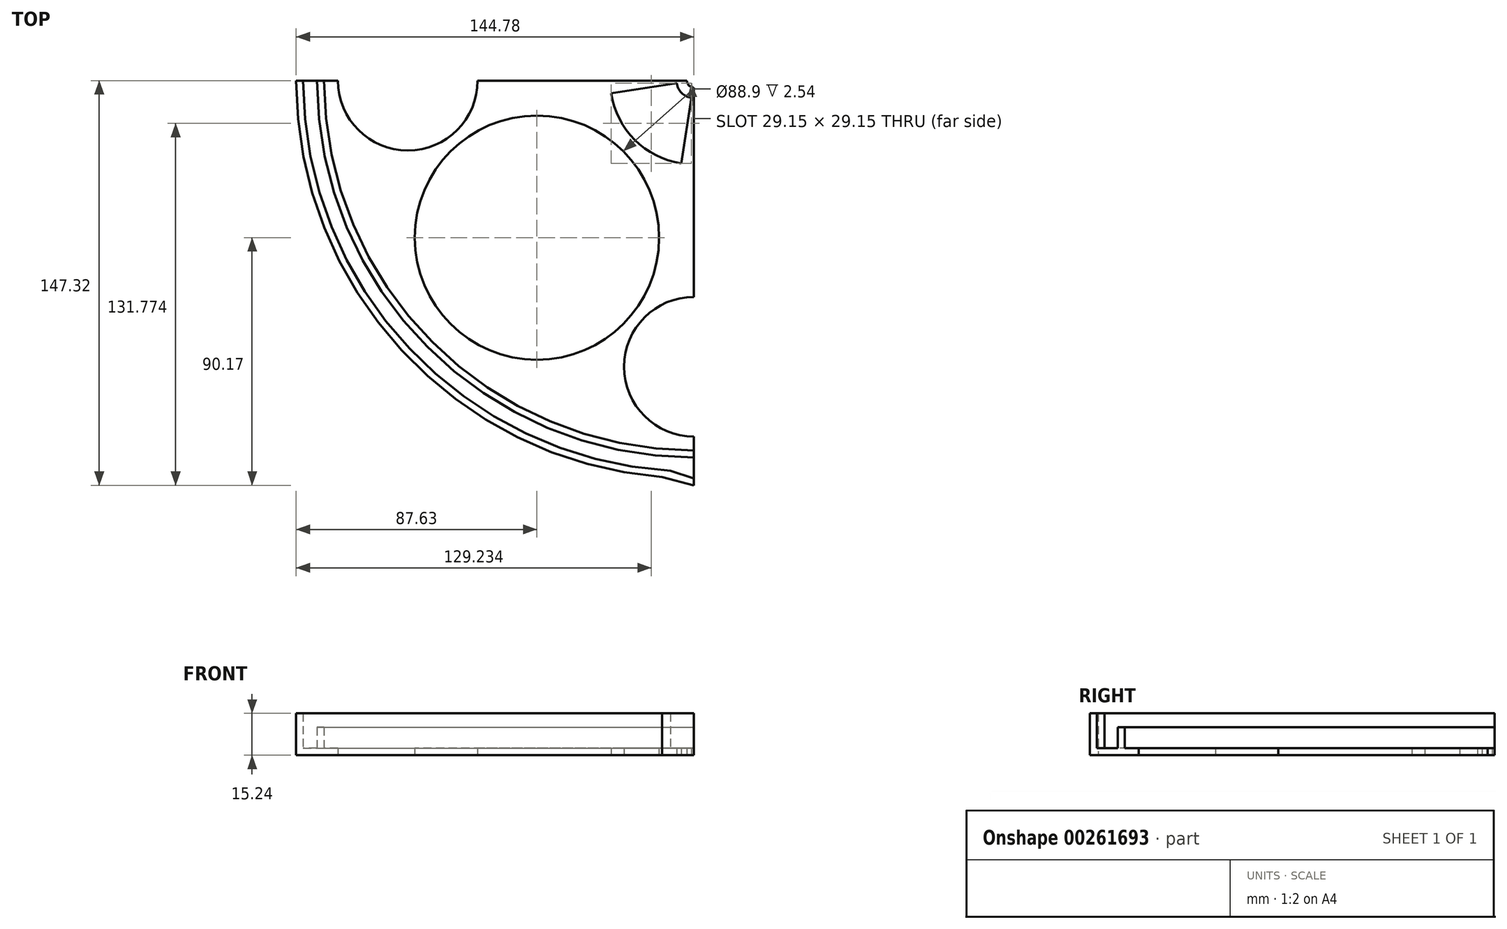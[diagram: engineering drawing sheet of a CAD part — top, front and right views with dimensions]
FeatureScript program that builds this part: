
annotation { "Feature Type Name" : "Feature", "Feature Type Description" : "" }
export const myFeature = defineFeature(function(context is Context, id is Id, definition is map)
    precondition{}
    {
        {
            var Q0;
            Q0=qCreatedBy(makeId("Top.planeOp"),FACE);
            var sketch = newSketch(context, id + "F0", { "sketchPlane" : qUnion([Q0])});
            skCircle(sketch, "E0", {"center": v(0, 0) * mm, "radius": 134.62 * mm});
            skCircle(sketch, "E1.0", {"center": v(0, 0) * mm, "radius": 137.16 * mm});
            skCircle(sketch, "E2.0", {"center": v(0, 0) * mm, "radius": 144.78 * mm});
            skCircle(sketch, "E3.0", {"center": v(0, 0) * mm, "radius": 142.24 * mm});
            skCircle(sketch, "E4.0", {"center": v(0, 0) * mm, "radius": 2.54 * mm});
            skLineSegment(sketch, "E5", {"start": v(0, 0) * mm, "end": v(0, -147.32) * mm});
            skLineSegment(sketch, "E6", {"start": v(-11.57, -144.32) * mm, "end": v(0, -147.32) * mm});
            skFitSpline(sketch, "E7", {"points": [v(0, -147.32) * mm, v(5.92, -144.66) * mm], "startDerivative": vector(10.02, -2.47) * mm, "endDerivative": vector(12.8, 0.33) * mm});
            skLineSegment(sketch, "E8", {"start": v(-8.6, -141.98) * mm, "end": v(0, -144.78) * mm});
            skFitSpline(sketch, "E9", {"points": [v(0, -144.78) * mm, v(4.46, -142.17) * mm], "startDerivative": vector(6.28, -2.02) * mm, "endDerivative": vector(5.88, 0.14) * mm});
            skLineSegment(sketch, "E10", {"start": v(0, 0) * mm, "end": v(-144.78, 0) * mm});
            skLineSegment(sketch, "E11", {"start": v(0, 0) * mm, "end": v(0, 144.78) * mm});
            skLineSegment(sketch, "E12", {"start": v(0, 0) * mm, "end": v(144.78, 0) * mm});
            skLineSegment(sketch, "E13", {"start": v(0, -12.7) * mm, "end": v(-144.22, -12.7) * mm});
            skLineSegment(sketch, "E14", {"start": v(0, -12.7) * mm, "end": v(144.78, -12.7) * mm});
            skLineSegment(sketch, "E15", {"start": v(0, 12.7) * mm, "end": v(-144.22, 12.7) * mm});
            skLineSegment(sketch, "E16", {"start": v(0, 12.7) * mm, "end": v(144.78, 12.7) * mm});
            skLineSegment(sketch, "E17", {"start": v(-12.7, 0) * mm, "end": v(-12.7, 144.22) * mm});
            skLineSegment(sketch, "E18", {"start": v(12.7, 0) * mm, "end": v(12.7, 144.22) * mm});
            skLineSegment(sketch, "E19", {"start": v(-12.7, 0) * mm, "end": v(-12.7, -144.22) * mm});
            skLineSegment(sketch, "E20", {"start": v(12.7, 0) * mm, "end": v(12.7, -144.22) * mm});
            skCircle(sketch, "E21", {"center": v(-57.15, -57.15) * mm, "radius": 44.45 * mm});
            skCircle(sketch, "E22", {"center": v(57.15, -57.15) * mm, "radius": 44.45 * mm});
            skCircle(sketch, "E23", {"center": v(-57.15, 57.15) * mm, "radius": 44.45 * mm});
            skCircle(sketch, "E24", {"center": v(57.15, 57.15) * mm, "radius": 44.45 * mm});
            skCircle(sketch, "E25", {"center": v(-104.14, 0) * mm, "radius": 25.4 * mm});
            skCircle(sketch, "E26", {"center": v(0, 104.14) * mm, "radius": 25.4 * mm});
            skCircle(sketch, "E27", {"center": v(104.14, 0) * mm, "radius": 25.4 * mm});
            skCircle(sketch, "E28", {"center": v(0, -104.14) * mm, "radius": 25.4 * mm});
            skCircle(sketch, "E29", {"center": v(0, 0) * mm, "radius": 30.48 * mm});
            skLineSegment(sketch, "E30", {"start": v(-12.7, -82.14) * mm, "end": v(0, 0) * mm});
            skLineSegment(sketch, "E31", {"start": v(12.7, -82.14) * mm, "end": v(0, 0) * mm});
            skLineSegment(sketch, "E32", {"start": v(82.14, -12.7) * mm, "end": v(0, 0) * mm});
            skLineSegment(sketch, "E33", {"start": v(82.14, 12.7) * mm, "end": v(0, 0) * mm});
            skLineSegment(sketch, "E34", {"start": v(12.7, 82.14) * mm, "end": v(0, 0) * mm});
            skLineSegment(sketch, "E35", {"start": v(-12.7, 82.14) * mm, "end": v(0, 0) * mm});
            skLineSegment(sketch, "E36", {"start": v(-82.14, -12.7) * mm, "end": v(0, 0) * mm});
            skLineSegment(sketch, "E37", {"start": v(-82.14, 12.7) * mm, "end": v(0, 0) * mm});
            skCircle(sketch, "E38", {"center": v(0, 0) * mm, "radius": 6.35 * mm});
            skSolve(sketch);
        }
        {
            var Q0;
            {var subQ0=sQuery(id+"F0.wireOp",EDGE,"E5");var subQ1=sQuery(id+"F0.wireOp",EDGE,"E0");var subQ2=makeQuery(id+"F0.imprint","INTERSECT",VERTEX,{"derivedFrom":[subQ1,subQ0]});Q0=makeQuery(id+"F0.imprint","IMPRINT",FACE,{"disambiguationData":[TD([[makeQuery(id+"F0.imprint","IMPRINT",EDGE,{"disambiguationData":[TD([[subQ2,1.0]])],"derivedFrom":subQ1}),1.0]])]});}
            var Q1;
            {var subQ0=sQuery(id+"F0.wireOp",EDGE,"E13");var subQ1=sQuery(id+"F0.wireOp",EDGE,"E0");var subQ2=makeQuery(id+"F0.imprint","INTERSECT",VERTEX,{"derivedFrom":[subQ1,subQ0]});Q1=makeQuery(id+"F0.imprint","IMPRINT",FACE,{"disambiguationData":[TD([[makeQuery(id+"F0.imprint","IMPRINT",EDGE,{"disambiguationData":[TD([[subQ2,-1.0]])],"derivedFrom":subQ1}),1.0]])]});}
            var Q2;
            {var subQ1=sQuery(id+"F0.wireOp",EDGE,"E10");var subQ3=sQuery(id+"F0.wireOp",EDGE,"E4.0");var subQ4=makeQuery(id+"F0.imprint","INTERSECT",VERTEX,{"derivedFrom":[subQ3,subQ1]});Q2=makeQuery(id+"F0.imprint","IMPRINT",FACE,{"disambiguationData":[TD([[makeQuery(id+"F0.imprint","IMPRINT",EDGE,{"disambiguationData":[TD([[subQ4,-1.0]])],"derivedFrom":subQ3}),-1.0]])]});}
            var Q3;
            {var subQ4=sQuery(id+"F0.wireOp",EDGE,"E10");var subQ6=sQuery(id+"F0.wireOp",EDGE,"E0");var subQ7=makeQuery(id+"F0.imprint","INTERSECT",VERTEX,{"derivedFrom":[subQ6,subQ4]});Q3=makeQuery(id+"F0.imprint","IMPRINT",FACE,{"disambiguationData":[TD([[makeQuery(id+"F0.imprint","IMPRINT",EDGE,{"disambiguationData":[TD([[subQ7,-1.0]])],"derivedFrom":subQ6}),1.0]])]});}
            var Q4;
            {var subQ0=sQuery(id+"F0.wireOp",EDGE,"E29");var subQ1=sQuery(id+"F0.wireOp",EDGE,"E13");var subQ2=makeQuery(id+"F0.imprint","INTERSECT",VERTEX,{"derivedFrom":[subQ1,subQ0]});Q4=makeQuery(id+"F0.imprint","IMPRINT",FACE,{"disambiguationData":[TD([[makeQuery(id+"F0.imprint","IMPRINT",EDGE,{"disambiguationData":[TD([[subQ2,-1.0]])],"derivedFrom":subQ1}),1.0]])]});}
            var Q5;
            {var subQ0=sQuery(id+"F0.wireOp",EDGE,"E29");var subQ1=sQuery(id+"F0.wireOp",EDGE,"E13");var subQ2=makeQuery(id+"F0.imprint","INTERSECT",VERTEX,{"derivedFrom":[subQ1,subQ0]});Q5=makeQuery(id+"F0.imprint","IMPRINT",FACE,{"disambiguationData":[TD([[makeQuery(id+"F0.imprint","IMPRINT",EDGE,{"disambiguationData":[TD([[subQ2,-1.0]])],"derivedFrom":subQ1}),-1.0]])]});}
            var Q6;
            {var subQ0=sQuery(id+"F0.wireOp",EDGE,"E29");var subQ1=sQuery(id+"F0.wireOp",EDGE,"E19");var subQ2=makeQuery(id+"F0.imprint","INTERSECT",VERTEX,{"derivedFrom":[subQ1,subQ0]});Q6=makeQuery(id+"F0.imprint","IMPRINT",FACE,{"disambiguationData":[TD([[makeQuery(id+"F0.imprint","IMPRINT",EDGE,{"disambiguationData":[TD([[subQ2,-1.0]])],"derivedFrom":subQ1}),1.0]])]});}
            var Q7;
            {var subQ0=sQuery(id+"F0.wireOp",EDGE,"E29");var subQ1=sQuery(id+"F0.wireOp",EDGE,"E5");var subQ2=makeQuery(id+"F0.imprint","INTERSECT",VERTEX,{"derivedFrom":[subQ1,subQ0]});Q7=makeQuery(id+"F0.imprint","IMPRINT",FACE,{"disambiguationData":[TD([[makeQuery(id+"F0.imprint","IMPRINT",EDGE,{"disambiguationData":[TD([[subQ2,-1.0]])],"derivedFrom":subQ1}),-1.0]])]});}
            var Q8;
            {var subQ1=sQuery(id+"F0.wireOp",EDGE,"E5");var subQ3=sQuery(id+"F0.wireOp",EDGE,"E29");var subQ4=makeQuery(id+"F0.imprint","INTERSECT",VERTEX,{"derivedFrom":[subQ1,subQ3]});Q8=makeQuery(id+"F0.imprint","IMPRINT",FACE,{"disambiguationData":[TD([[makeQuery(id+"F0.imprint","IMPRINT",EDGE,{"disambiguationData":[TD([[subQ4,1.0]])],"derivedFrom":subQ3}),1.0]])]});}
            var Q9;
            {var subQ0=sQuery(id+"F0.wireOp",EDGE,"E13");var subQ5=sQuery(id+"F0.wireOp",EDGE,"E30");var subQ6=makeQuery(id+"F0.imprint","INTERSECT",VERTEX,{"derivedFrom":[subQ0,subQ5]});Q9=makeQuery(id+"F0.imprint","IMPRINT",FACE,{"disambiguationData":[TD([[makeQuery(id+"F0.imprint","IMPRINT",EDGE,{"disambiguationData":[TD([[subQ6,-1.0]])],"derivedFrom":subQ5}),-1.0]])]});}
            var Q10;
            {var subQ0=sQuery(id+"F0.wireOp",EDGE,"E30");var subQ1=sQuery(id+"F0.wireOp",EDGE,"E4.0");var subQ2=makeQuery(id+"F0.imprint","INTERSECT",VERTEX,{"derivedFrom":[subQ1,subQ0]});Q10=makeQuery(id+"F0.imprint","IMPRINT",FACE,{"disambiguationData":[TD([[makeQuery(id+"F0.imprint","IMPRINT",EDGE,{"disambiguationData":[TD([[subQ2,-1.0]])],"derivedFrom":subQ1}),-1.0]])]});}
            var Q11;
            {var subQ0=sQuery(id+"F0.wireOp",EDGE,"E36");var subQ1=sQuery(id+"F0.wireOp",EDGE,"E4.0");var subQ2=makeQuery(id+"F0.imprint","INTERSECT",VERTEX,{"derivedFrom":[subQ1,subQ0]});Q11=makeQuery(id+"F0.imprint","IMPRINT",FACE,{"disambiguationData":[TD([[makeQuery(id+"F0.imprint","IMPRINT",EDGE,{"disambiguationData":[TD([[subQ2,-1.0]])],"derivedFrom":subQ1}),-1.0]])]});}
            var Q12;
            {var subQ1=sQuery(id+"F0.wireOp",EDGE,"E10");var subQ3=sQuery(id+"F0.wireOp",EDGE,"E29");var subQ4=makeQuery(id+"F0.imprint","INTERSECT",VERTEX,{"derivedFrom":[subQ1,subQ3]});Q12=makeQuery(id+"F0.imprint","IMPRINT",FACE,{"disambiguationData":[TD([[makeQuery(id+"F0.imprint","IMPRINT",EDGE,{"disambiguationData":[TD([[subQ4,-1.0]])],"derivedFrom":subQ3}),1.0]])]});}
            var Q13;
            {var subQ0=sQuery(id+"F0.wireOp",EDGE,"E19");var subQ5=sQuery(id+"F0.wireOp",EDGE,"E36");var subQ6=makeQuery(id+"F0.imprint","INTERSECT",VERTEX,{"derivedFrom":[subQ0,subQ5]});Q13=makeQuery(id+"F0.imprint","IMPRINT",FACE,{"disambiguationData":[TD([[makeQuery(id+"F0.imprint","IMPRINT",EDGE,{"disambiguationData":[TD([[subQ6,-1.0]])],"derivedFrom":subQ5}),1.0]])]});}
            var Q14;
            {var subQ0=sQuery(id+"F0.wireOp",EDGE,"E29");var subQ1=sQuery(id+"F0.wireOp",EDGE,"E10");var subQ2=makeQuery(id+"F0.imprint","INTERSECT",VERTEX,{"derivedFrom":[subQ1,subQ0]});Q14=makeQuery(id+"F0.imprint","IMPRINT",FACE,{"disambiguationData":[TD([[makeQuery(id+"F0.imprint","IMPRINT",EDGE,{"disambiguationData":[TD([[subQ2,-1.0]])],"derivedFrom":subQ1}),1.0]])]});}
            extrude(context, id + "F1", {"entities" : qUnion([Q0, Q1, Q2, Q3, Q4, Q5, Q6, Q7, Q8, Q9, Q10, Q11, Q12, Q13, Q14]), "depth" : 2.54 * mm});
        }
        {
            var Q0;
            {var subQ0=sQuery(id+"F0.wireOp",EDGE,"E5");var subQ1=sQuery(id+"F0.wireOp",EDGE,"E0");var subQ2=makeQuery(id+"F0.imprint","INTERSECT",VERTEX,{"derivedFrom":[subQ1,subQ0]});Q0=makeQuery(id+"F0.imprint","IMPRINT",FACE,{"disambiguationData":[TD([[makeQuery(id+"F0.imprint","IMPRINT",EDGE,{"disambiguationData":[TD([[subQ2,1.0]])],"derivedFrom":subQ1}),-1.0]])]});}
            var Q1;
            {var subQ0=sQuery(id+"F0.wireOp",EDGE,"E13");var subQ1=sQuery(id+"F0.wireOp",EDGE,"E0");var subQ2=makeQuery(id+"F0.imprint","INTERSECT",VERTEX,{"derivedFrom":[subQ1,subQ0]});Q1=makeQuery(id+"F0.imprint","IMPRINT",FACE,{"disambiguationData":[TD([[makeQuery(id+"F0.imprint","IMPRINT",EDGE,{"disambiguationData":[TD([[subQ2,-1.0]])],"derivedFrom":subQ1}),-1.0]])]});}
            var Q2;
            {var subQ0=sQuery(id+"F0.wireOp",EDGE,"E10");var subQ1=sQuery(id+"F0.wireOp",EDGE,"E0");var subQ2=makeQuery(id+"F0.imprint","INTERSECT",VERTEX,{"derivedFrom":[subQ1,subQ0]});Q2=makeQuery(id+"F0.imprint","IMPRINT",FACE,{"disambiguationData":[TD([[makeQuery(id+"F0.imprint","IMPRINT",EDGE,{"disambiguationData":[TD([[subQ2,-1.0]])],"derivedFrom":subQ1}),-1.0]])]});}
            extrude(context, id + "F2", {"entities" : qUnion([Q0, Q1, Q2]), "operationType" : NewBodyOperationType.ADD, "depth" : 10.16 * mm});
        }
        {
            var Q0;
            {var subQ0=sQuery(id+"F0.wireOp",EDGE,"E5");var subQ1=sQuery(id+"F0.wireOp",EDGE,"E1.0");var subQ2=makeQuery(id+"F0.imprint","INTERSECT",VERTEX,{"derivedFrom":[subQ1,subQ0]});Q0=makeQuery(id+"F0.imprint","IMPRINT",FACE,{"disambiguationData":[TD([[makeQuery(id+"F0.imprint","IMPRINT",EDGE,{"disambiguationData":[TD([[subQ2,1.0]])],"derivedFrom":subQ1}),-1.0]])]});}
            var Q1;
            {var subQ0=sQuery(id+"F0.wireOp",EDGE,"E8");Q1=makeQuery(id+"F0.imprint","IMPRINT",FACE,{"disambiguationData":[TD([[makeQuery(id+"F0.imprint","IMPRINT",EDGE,{"derivedFrom":subQ0}),1.0]])]});}
            var Q2;
            {var subQ0=sQuery(id+"F0.wireOp",EDGE,"E13");var subQ1=sQuery(id+"F0.wireOp",EDGE,"E1.0");var subQ2=makeQuery(id+"F0.imprint","INTERSECT",VERTEX,{"derivedFrom":[subQ1,subQ0]});Q2=makeQuery(id+"F0.imprint","IMPRINT",FACE,{"disambiguationData":[TD([[makeQuery(id+"F0.imprint","IMPRINT",EDGE,{"disambiguationData":[TD([[subQ2,-1.0]])],"derivedFrom":subQ1}),-1.0]])]});}
            var Q3;
            {var subQ0=sQuery(id+"F0.wireOp",EDGE,"E10");var subQ1=sQuery(id+"F0.wireOp",EDGE,"E1.0");var subQ2=makeQuery(id+"F0.imprint","INTERSECT",VERTEX,{"derivedFrom":[subQ1,subQ0]});Q3=makeQuery(id+"F0.imprint","IMPRINT",FACE,{"disambiguationData":[TD([[makeQuery(id+"F0.imprint","IMPRINT",EDGE,{"disambiguationData":[TD([[subQ2,-1.0]])],"derivedFrom":subQ1}),-1.0]])]});}
            extrude(context, id + "F3", {"entities" : qUnion([Q0, Q1, Q2, Q3]), "operationType" : NewBodyOperationType.ADD, "depth" : 2.54 * mm});
        }
        {
            var Q0;
            {var subQ5=sQuery(id+"F0.wireOp",EDGE,"E2.0");var subQ9=makeQuery(id+"F0.imprint","INTERSECT",VERTEX,{"derivedFrom":[subQ5,sQuery(id+"F0.wireOp",EDGE,"E6")]});Q0=makeQuery(id+"F0.imprint","IMPRINT",FACE,{"disambiguationData":[TD([[makeQuery(id+"F0.imprint","IMPRINT",EDGE,{"disambiguationData":[TD([[subQ9,-1.0]])],"derivedFrom":subQ5}),1.0]])]});}
            var Q1;
            {var subQ0=sQuery(id+"F0.wireOp",EDGE,"E6");Q1=makeQuery(id+"F0.imprint","IMPRINT",FACE,{"disambiguationData":[TD([[makeQuery(id+"F0.imprint","IMPRINT",EDGE,{"derivedFrom":subQ0}),1.0]])]});}
            var Q2;
            {var subQ0=sQuery(id+"F0.wireOp",EDGE,"E13");var subQ1=sQuery(id+"F0.wireOp",EDGE,"E2.0");var subQ2=makeQuery(id+"F0.imprint","INTERSECT",VERTEX,{"derivedFrom":[subQ1,subQ0]});Q2=makeQuery(id+"F0.imprint","IMPRINT",FACE,{"disambiguationData":[TD([[makeQuery(id+"F0.imprint","IMPRINT",EDGE,{"disambiguationData":[TD([[subQ2,-1.0]])],"derivedFrom":subQ1}),1.0]])]});}
            var Q3;
            {var subQ0=sQuery(id+"F0.wireOp",EDGE,"E10");var subQ1=sQuery(id+"F0.wireOp",EDGE,"E2.0");var subQ2=makeQuery(id+"F0.imprint","INTERSECT",VERTEX,{"derivedFrom":[subQ1,subQ0]});Q3=makeQuery(id+"F0.imprint","IMPRINT",FACE,{"disambiguationData":[TD([[makeQuery(id+"F0.imprint","IMPRINT",EDGE,{"disambiguationData":[TD([[subQ2,-1.0]])],"derivedFrom":subQ1}),1.0]])]});}
            extrude(context, id + "F4", {"entities" : qUnion([Q0, Q1, Q2, Q3]), "operationType" : NewBodyOperationType.ADD, "depth" : 15.24 * mm});
        }
    });
